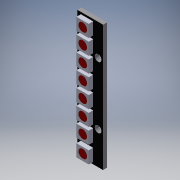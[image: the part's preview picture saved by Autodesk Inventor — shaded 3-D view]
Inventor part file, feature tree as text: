
AUTODESK INVENTOR PART (.ipt)
format: ipt  version: 2016 (Build 200138000, 138)  size: 243,712 bytes
history: native  units: in
note: dims shown in document units (in); Inventor stores cm internally (conversion verified against a paired STEP export)
features: extrude x4, sketch x4
ambient origin geometry x8: Origin, YZ Plane, XZ Plane, XY Plane, X Axis, Y Axis, Z Axis, Center Point
bodies: Solid1 (feature_tree)
feature tree (8):
  extrude  "Extrusion1"  Depth=2.0in
  extrude  "Extrusion2"  Depth=0.05in
  extrude  "Extrusion3"  Depth=0.13in
  extrude  "Extrusion4"  Depth=0.065in
  sketch  "Sketch1"  dims[d0=0.41in d1=2.0in]
  sketch  "Sketch2"  dims[d2=0.065in d3=0.0in d4=0.05in]
  sketch  "Sketch3"  dims[d5=0.13in d6=0.14in]
  sketch  "Sketch4"  dims[d7=0.13in d8=0.14in d9=0.245in d10=0.245in d11=0.245in d12=0.245in d13=0.245in d14=0.245in d15=0.14in d16=0.14in d17=0.14in d18=0.14in d19=0.14in d20=0.14in d21=0.195in d22=0.195in d23=0.195in d24=0.195in d25=0.195in d26=0.195in d27=0.195in d28=0.195in d29=0.195in d30=0.195in d31=0.195in d32=0.195in d33=0.07in d34=0.0in d35=0.065in d36=0.0in d37=0.065in d38=0.0in]
